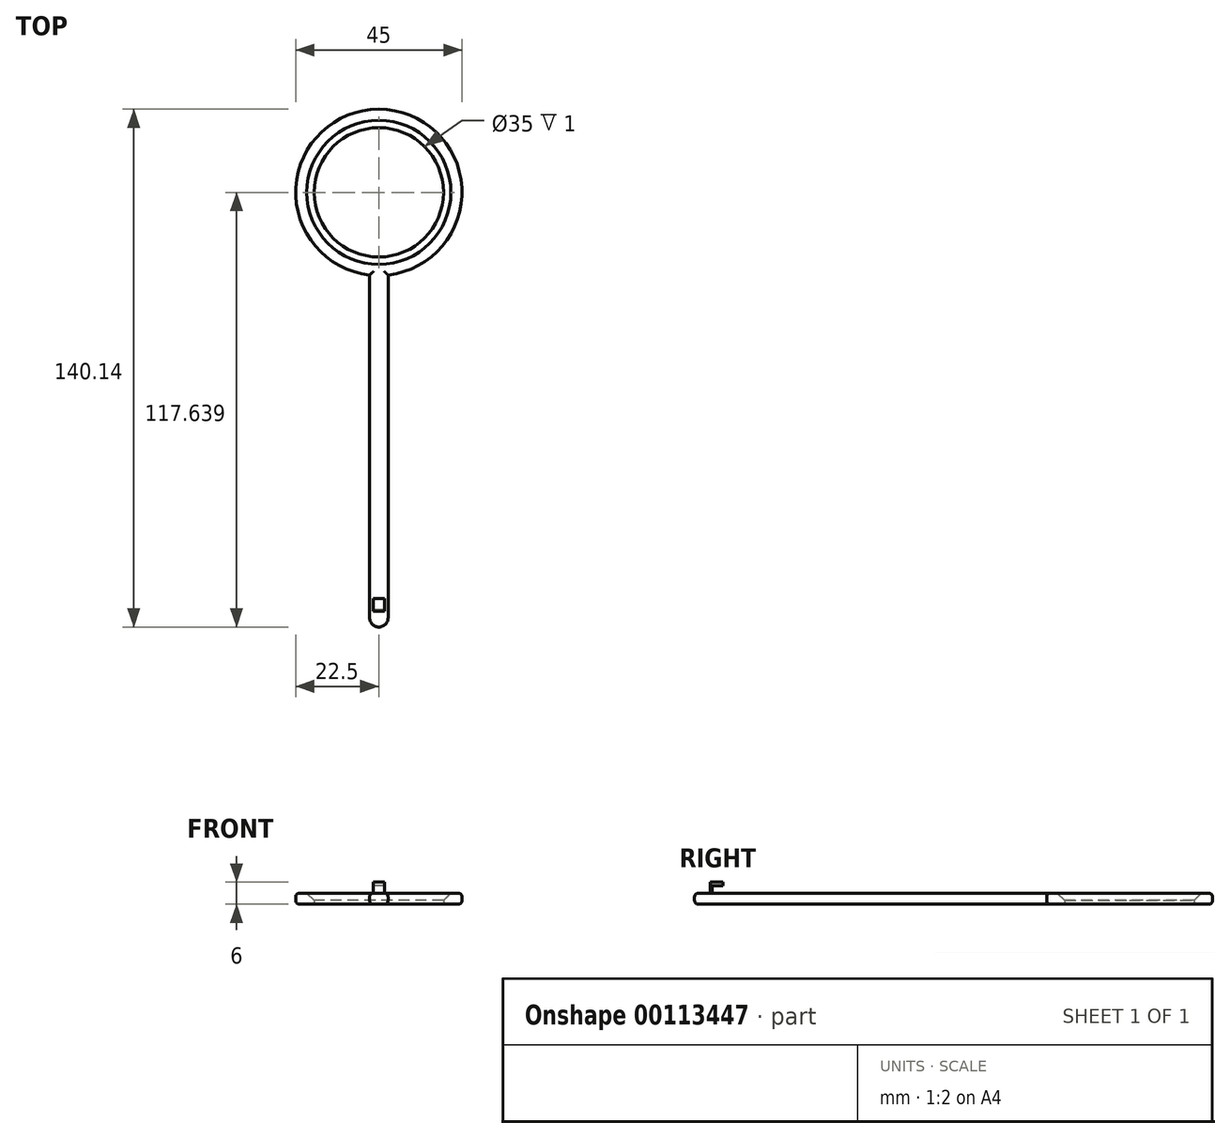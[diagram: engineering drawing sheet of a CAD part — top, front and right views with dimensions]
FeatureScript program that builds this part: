
annotation { "Feature Type Name" : "Feature", "Feature Type Description" : "" }
export const myFeature = defineFeature(function(context is Context, id is Id, definition is map)
    precondition{}
    {
        {
            var Q0;
            Q0=qCreatedBy(makeId("Top.planeOp"),FACE);
            var sketch = newSketch(context, id + "F0", { "sketchPlane" : qUnion([Q0])});
            skLineSegment(sketch, "E0.bottom", {"start": v(2.5, 70) * mm, "end": v(-2.5, 70) * mm});
            skLineSegment(sketch, "E0.top", {"start": v(2.5, -70) * mm, "end": v(-2.5, -70) * mm});
            skLineSegment(sketch, "E0.left", {"start": v(2.5, 70) * mm, "end": v(2.5, -70) * mm});
            skLineSegment(sketch, "E0.right", {"start": v(-2.5, 70) * mm, "end": v(-2.5, -70) * mm});
            skPoint(sketch, "E0.middle", {"position": v(0, 0) * mm});
            skCircle(sketch, "E1", {"center": v(0, 47.64) * mm, "radius": 22.5 * mm});
            skPoint(sketch, "E1.third.point", {"position": v(16.15, 31.97) * mm});
            skCircle(sketch, "E2", {"center": v(0, 47.64) * mm, "radius": 17.5 * mm});
            skLineSegment(sketch, "E3", {"start": v(-2.5, -67.5) * mm, "end": v(2.5, -67.5) * mm, "construction": true});
            skArc(sketch, "E4", {"start": v(-2.5, -67.5) * mm, "mid": v(0, -70) * mm, "end": v(2.5, -67.5) * mm});
            skLineSegment(sketch, "E5", {"start": v(-2.5, -65.5) * mm, "end": v(2.5, -65.5) * mm});
            skLineSegment(sketch, "E6.bottom", {"start": v(1.5, -65.27) * mm, "end": v(-1.5, -65.27) * mm});
            skLineSegment(sketch, "E6.top", {"start": v(1.5, -65.73) * mm, "end": v(-1.5, -65.73) * mm});
            skLineSegment(sketch, "E6.left", {"start": v(1.5, -65.27) * mm, "end": v(1.5, -65.73) * mm});
            skLineSegment(sketch, "E6.right", {"start": v(-1.5, -65.27) * mm, "end": v(-1.5, -65.73) * mm});
            skPoint(sketch, "E6.middle", {"position": v(0, -65.5) * mm});
            skSolve(sketch);
        }
        {
            var Q0;
            {var subQ0=sQuery(id+"F0.wireOp",EDGE,"E0.bottom");Q0=makeQuery(id+"F0.imprint","IMPRINT",FACE,{"disambiguationData":[TD([[makeQuery(id+"F0.imprint","IMPRINT",EDGE,{"derivedFrom":subQ0}),-1.0]])]});}
            var Q1;
            {var subQ0=sQuery(id+"F0.wireOp",EDGE,"E1");var subQ1=sQuery(id+"F0.wireOp",EDGE,"E0.left");var subQ6=makeQuery(id+"F0.imprint","INTERSECT",VERTEX,{"derivedFrom":[subQ1,subQ0]});Q1=makeQuery(id+"F0.imprint","IMPRINT",FACE,{"disambiguationData":[TD([[makeQuery(id+"F0.imprint","IMPRINT",EDGE,{"disambiguationData":[TD([[subQ6,1.0]])],"derivedFrom":subQ1}),1.0]])]});}
            var Q2;
            {var subQ0=sQuery(id+"F0.wireOp",EDGE,"E1");var subQ1=sQuery(id+"F0.wireOp",EDGE,"E0.right");var subQ5=makeQuery(id+"F0.imprint","INTERSECT",VERTEX,{"derivedFrom":[subQ1,subQ0]});Q2=makeQuery(id+"F0.imprint","IMPRINT",FACE,{"disambiguationData":[TD([[makeQuery(id+"F0.imprint","IMPRINT",EDGE,{"disambiguationData":[TD([[subQ5,1.0]])],"derivedFrom":subQ1}),-1.0]])]});}
            var Q3;
            {var subQ0=sQuery(id+"F0.wireOp",EDGE,"E0.bottom");Q3=makeQuery(id+"F0.imprint","IMPRINT",FACE,{"disambiguationData":[TD([[makeQuery(id+"F0.imprint","IMPRINT",EDGE,{"derivedFrom":subQ0}),1.0]])]});}
            var Q4;
            {var subQ0=sQuery(id+"F0.wireOp",EDGE,"E1");var subQ1=sQuery(id+"F0.wireOp",EDGE,"E0.left");var subQ2=makeQuery(id+"F0.imprint","INTERSECT",VERTEX,{"derivedFrom":[subQ1,subQ0]});Q4=makeQuery(id+"F0.imprint","IMPRINT",FACE,{"disambiguationData":[TD([[makeQuery(id+"F0.imprint","IMPRINT",EDGE,{"disambiguationData":[TD([[subQ2,1.0]])],"derivedFrom":subQ1}),-1.0]])]});}
            var Q5;
            {var subQ1=sQuery(id+"F0.wireOp",EDGE,"E0.left");var subQ5=sQuery(id+"F0.wireOp",EDGE,"E4");var subQ8=makeQuery(id+"F0.imprint","INTERSECT",VERTEX,{"derivedFrom":[subQ1,subQ5]});Q5=makeQuery(id+"F0.imprint","IMPRINT",FACE,{"disambiguationData":[TD([[makeQuery(id+"F0.imprint","IMPRINT",EDGE,{"disambiguationData":[TD([[subQ8,1.0]])],"derivedFrom":subQ1}),-1.0]])]});}
            var Q6;
            {var subQ12=sQuery(id+"F0.wireOp",EDGE,"E6.bottom");Q6=makeQuery(id+"F0.imprint","IMPRINT",FACE,{"disambiguationData":[TD([[makeQuery(id+"F0.imprint","IMPRINT",EDGE,{"derivedFrom":subQ12}),-1.0]])]});}
            extrude(context, id + "F1", {"entities" : qUnion([Q0, Q1, Q2, Q3, Q4, Q5, Q6]), "depth" : 3 * mm});
        }
        {
            var Q0;
            Q0=makeQuery(id+"F0.imprint","IMPRINT",FACE,{"disambiguationData":[TD([[makeQuery(id+"F0.imprint","IMPRINT",EDGE,{"derivedFrom":sQuery(id+"F0.wireOp",EDGE,"VLeqMaEx-cvx1-G24x-PzgO-k9joTiTwyqwW.bottom")}),-1.0]])]});
            var Q1;
            {var subQ5=sQuery(id+"F0.wireOp",EDGE,"E6.bottom");Q1=makeQuery(id+"F0.imprint","IMPRINT",FACE,{"disambiguationData":[TD([[makeQuery(id+"F0.imprint","IMPRINT",EDGE,{"derivedFrom":subQ5}),1.0]])]});}
            var Q2;
            {var subQ5=sQuery(id+"F0.wireOp",EDGE,"E6.top");Q2=makeQuery(id+"F0.imprint","IMPRINT",FACE,{"disambiguationData":[TD([[makeQuery(id+"F0.imprint","IMPRINT",EDGE,{"derivedFrom":subQ5}),-1.0]])]});}
            extrude(context, id + "F2", {"entities" : qUnion([Q0, Q1, Q2]), "operationType" : NewBodyOperationType.ADD, "depth" : 6 * mm});
        }
        {
            var Q0;
            Q0=makeQuery(id+"F2.opExtrude","SWEPT_FACE",FACE,{"disambiguationData":[OSD([sQuery(id+"F0.wireOp",EDGE,"E6.bottom")])]});
            var sketch = newSketch(context, id + "F3", { "sketchPlane" : qUnion([Q0])});
            skPoint(sketch, "E7.end.orphan", {"position": v(0, 0) * mm});
            skLineSegment(sketch, "E8", {"start": v(0, 0) * mm, "end": v(1000, 0) * mm});
            skLineSegment(sketch, "E9", {"start": v(7.6, -79.7) * mm, "end": v(4.64, -79.7) * mm});
            skLineSegment(sketch, "E10", {"start": v(-1.5, 5) * mm, "end": v(1.5, 5) * mm});
            skSolve(sketch);
        }
        {
            var Q0;
            {var subQ0=sQuery(id+"F3.wireOp",EDGE,"E10");Q0=makeQuery(id+"F3.imprint","IMPRINT",FACE,{"disambiguationData":[TD([[makeQuery(id+"F3.imprint","IMPRINT",EDGE,{"derivedFrom":subQ0}),1.0]])]});}
            extrude(context, id + "F4", {"entities" : qUnion([Q0]), "operationType" : NewBodyOperationType.ADD, "depth" : 3 * mm});
        }
        {
            var Q0;
            Q0=makeQuery(id+"F1.opExtrude","CAP_EDGE",EDGE,{"disambiguationData":[OSD([sQuery(id+"F0.wireOp",EDGE,"E1")])],"isStart":false});
            var Q1;
            Q1=makeQuery(id+"F1.opExtrude","CAP_EDGE",EDGE,{"disambiguationData":[OSD([sQuery(id+"F0.wireOp",EDGE,"E1")])],"isStart":true});
            var Q2;
            Q2=makeQuery(id+"F1.opExtrude","CAP_EDGE",EDGE,{"disambiguationData":[OSD([sQuery(id+"F0.wireOp",EDGE,"E0.left")])],"isStart":true});
            var Q3;
            Q3=makeQuery(id+"F1.opExtrude","CAP_EDGE",EDGE,{"disambiguationData":[OSD([sQuery(id+"F0.wireOp",EDGE,"E0.left")])],"isStart":false});
            var Q4;
            Q4=makeQuery(id+"F1.opExtrude","CAP_EDGE",EDGE,{"disambiguationData":[OSD([sQuery(id+"F0.wireOp",EDGE,"E0.right")])],"isStart":false});
            var Q5;
            Q5=makeQuery(id+"F1.opExtrude","CAP_EDGE",EDGE,{"disambiguationData":[OSD([sQuery(id+"F0.wireOp",EDGE,"E0.right")])],"isStart":true});
            fillet(context, id + "F5", {"entities" : qUnion([Q0, Q1, Q2, Q3, Q4, Q5]), "radius" : 1 * mm, "tangentPropagation" : true, "allowEdgeOverflow" : false});
        }
        {
            var Q0;
            Q0=makeQuery(id+"F1.opExtrude","CAP_EDGE",EDGE,{"disambiguationData":[OSD([sQuery(id+"F0.wireOp",EDGE,"E2")])],"isStart":false});
            chamfer(context, id + "F6", {"entities" : qUnion([Q0]), "width" : 2 * mm, "tangentPropagation" : true});
        }
    });
